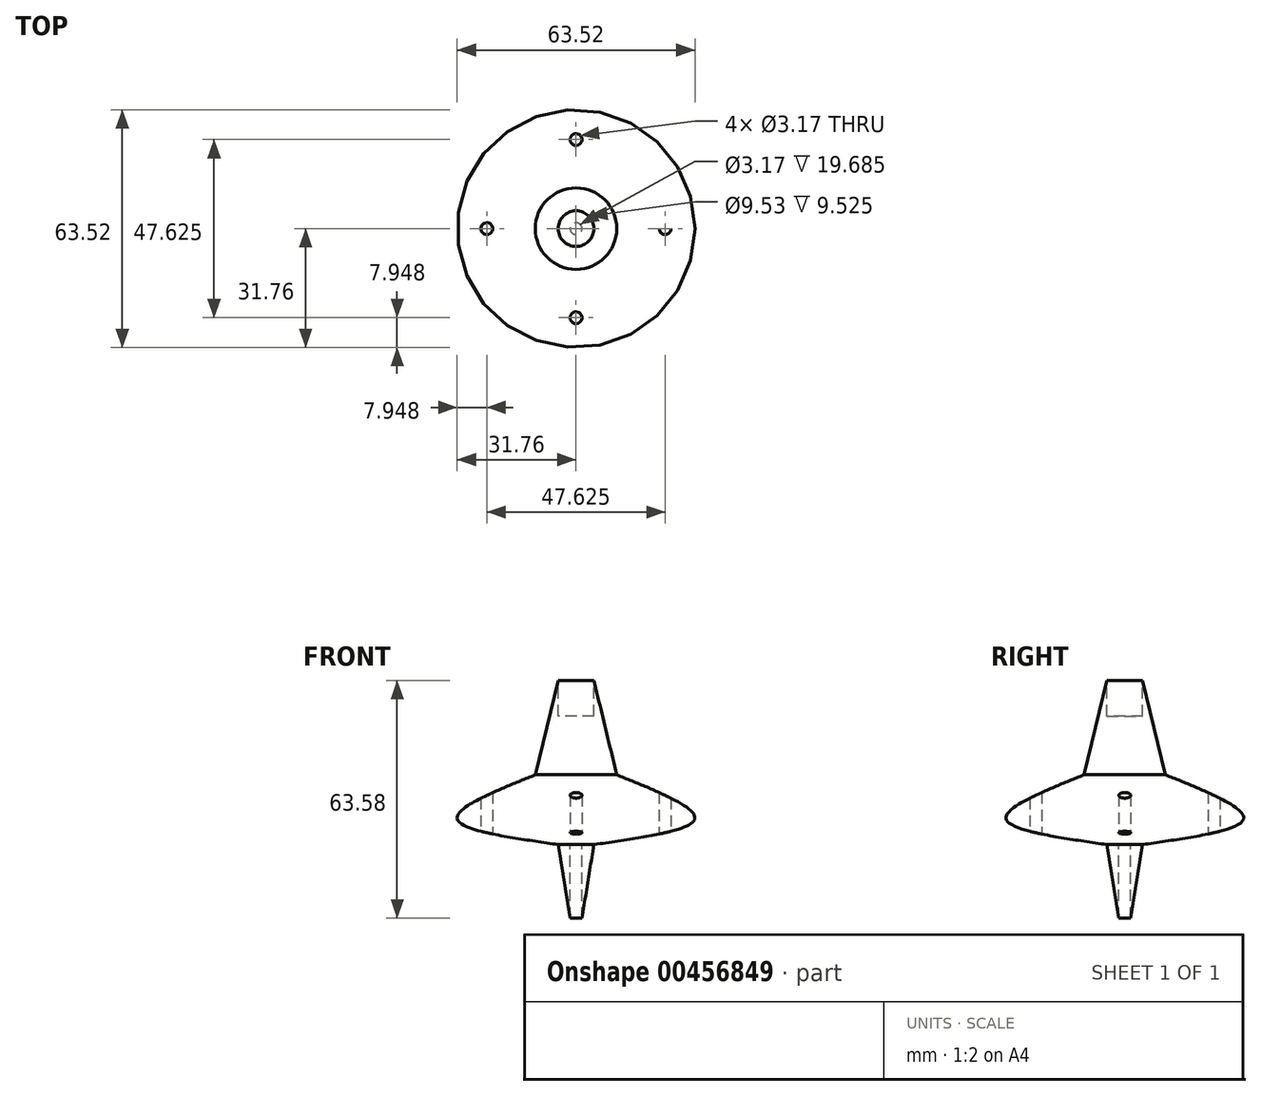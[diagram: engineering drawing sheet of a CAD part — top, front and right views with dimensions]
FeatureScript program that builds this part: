
annotation { "Feature Type Name" : "Feature", "Feature Type Description" : "" }
export const myFeature = defineFeature(function(context is Context, id is Id, definition is map)
    precondition{}
    {
        {
            var Q0;
            Q0=qCreatedBy(makeId("Front.planeOp"),FACE);
            var sketch = newSketch(context, id + "F0", { "sketchPlane" : qUnion([Q0])});
            skLineSegment(sketch, "E0", {"start": v(1.59, 19.69) * mm, "end": v(1.59, 0) * mm});
            skFitSpline(sketch, "E1", {"points": [v(4.76, 19.69) * mm, v(31.75, 26.67) * mm, v(10.88, 38.35) * mm], "startDerivative": vector(73.89, 10.97) * mm, "endDerivative": vector(-65.5, 26.35) * mm});
            skLineSegment(sketch, "E2", {"start": v(4.76, 63.58) * mm, "end": v(4.76, 54.05) * mm});
            skLineSegment(sketch, "E3", {"start": v(4.76, 54.05) * mm, "end": v(0, 54.05) * mm});
            skLineSegment(sketch, "E4", {"start": v(0, 54.05) * mm, "end": v(0, 19.69) * mm});
            skLineSegment(sketch, "E5", {"start": v(0, 19.69) * mm, "end": v(1.59, 19.69) * mm});
            skLineSegment(sketch, "E6", {"start": v(4.76, 19.69) * mm, "end": v(1.59, 0) * mm});
            skLineSegment(sketch, "E7", {"start": v(4.76, 63.58) * mm, "end": v(10.88, 38.35) * mm});
            skSolve(sketch);
        }
        {
            var Q0;
            Q0=makeQuery(id+"F0.imprint","IMPRINT",FACE,{"disambiguationData":[TD([[makeQuery(id+"F0.imprint","IMPRINT",EDGE,{"derivedFrom":sQuery(id+"F0.wireOp",EDGE,"E0")}),1.0]])]});
            var Q1;
            Q1=sQuery(id+"F0.wireOp",EDGE,"E4");
            revolve(context, id + "F1", {"entities" : qUnion([Q0]), "axis" : qUnion([Q1]), "revolveType" : RevolveType.FULL});
        }
        {
            var Q0;
            Q0=qCreatedBy(makeId("Top.planeOp"),FACE);
            var sketch = newSketch(context, id + "F2", { "sketchPlane" : qUnion([Q0])});
            skLineSegment(sketch, "E8", {"start": v(0, 0) * mm, "end": v(23.81, 0) * mm});
            skLineSegment(sketch, "E9", {"start": v(0, 0) * mm, "end": v(0, 23.81) * mm});
            skLineSegment(sketch, "E10", {"start": v(0, 0) * mm, "end": v(-23.81, 0) * mm});
            skLineSegment(sketch, "E11", {"start": v(0, 0) * mm, "end": v(0, -23.81) * mm});
            skSolve(sketch);
        }
        {
            var Q0;
            Q0=sQuery(id+"F2.wireOp",VERTEX,"E9.end");
            var Q1;
            Q1=sQuery(id+"F2.wireOp",VERTEX,"E8.end");
            var Q2;
            Q2=sQuery(id+"F2.wireOp",VERTEX,"E11.end");
            var Q3;
            Q3=sQuery(id+"F2.wireOp",VERTEX,"E10.end");
            var Q4;
            Q4=makeQuery(id+"F1.opRevolve","SWEPT_BODY",BODY,{"disambiguationData":[OSD([sQuery(id+"F0.wireOp",EDGE,"E0"),sQuery(id+"F0.wireOp",EDGE,"E1"),sQuery(id+"F0.wireOp",EDGE,"E2"),sQuery(id+"F0.wireOp",EDGE,"E3"),sQuery(id+"F0.wireOp",EDGE,"E4"),sQuery(id+"F0.wireOp",EDGE,"E5"),sQuery(id+"F0.wireOp",EDGE,"E6"),sQuery(id+"F0.wireOp",EDGE,"E7")])]});
            hole(context, id + "F3", {"style" : HoleStyle.SIMPLE, "endStyle" : HoleEndStyle.THROUGH, "oppositeDirection" : true, "holeDiameter" : 3.17 * mm, "isTappedThrough" : true, "tappedDepth" : 12.7 * mm, "tapClearance" : 3, "locations" : qUnion([Q0, Q1, Q2, Q3]), "scope" : qUnion([Q4])});
        }
    });
